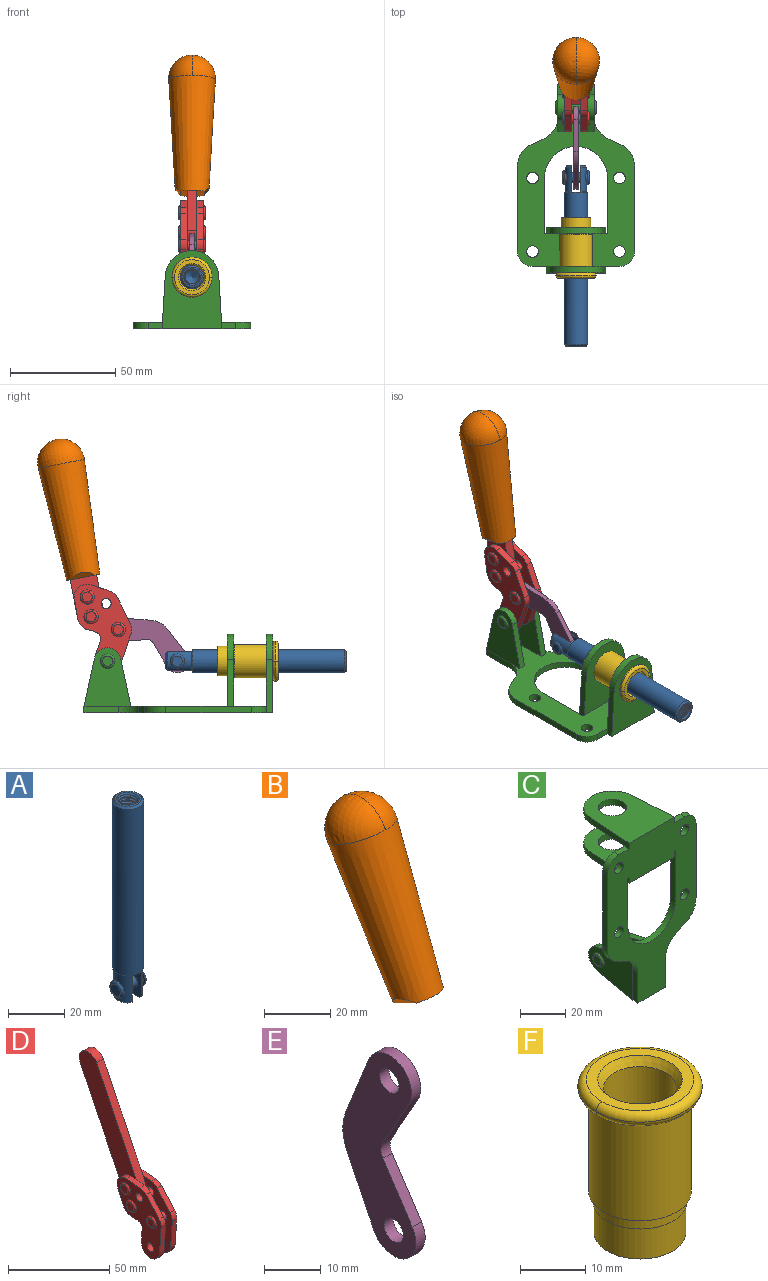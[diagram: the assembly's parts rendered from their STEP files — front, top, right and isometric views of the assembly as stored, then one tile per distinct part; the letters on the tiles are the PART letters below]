
ASSEMBLY  parts=6 mates=6
PART A: 48 faces, bbox 12.6x11.1x86.1 mm
  f0: torus R=2.41mm, axis (-1,0,0), area 15mm2, adj f30,f32,f34
  f1: torus R=2.41mm, axis (-1,0,0), area 15mm2, adj f29,f31,f33
  f2: cylinder r=5.54mm len=72.39mm, axis (0,0,1), area 2518.5mm2, adj f3,f4,f42,f43
  f3: cone r=5.54mm half-angle=45deg, axis (0,0,1), area 7.6mm2, adj f2,f5,f41
  f4: cone r=5.54mm half-angle=45deg, axis (0,0,-1), area 34.9mm2, adj f2,f39
  f5: cylinder r=5.08mm len=11.48mm, axis (0,0,1), area 108.3mm2, adj f3,f7,f8,f41
  f6: cylinder r=2.41mm len=4.83mm, axis (-1,0,0), area 71.2mm2, adj f40,f41
  f7: cylinder r=2.41mm len=4.83mm, axis (-1,0,0), area 7.6mm2, adj f5,f34
  f8: cone r=5.08mm half-angle=45deg, axis (0,0,1), area 10.6mm2, adj f5,f37,f41
  f9: cone r=3.98mm half-angle=45deg, axis (0,0,1), area 17.6mm2, adj f27,f39,f45,f46,f47
  f10: cylinder r=2.41mm len=4.83mm, axis (-1,0,0), area 7.6mm2, adj f33,f38
  f11: cylinder r=3.2mm len=6.4mm, axis (0,0,1), area 78.4mm2, adj f12,f28,f44,f45,f47
  f12: cylinder r=3.2mm len=6.4mm, axis (0,0,1), area 10.5mm2, adj f11,f13,f45,f47
  f13: cylinder r=3.2mm len=6.4mm, axis (0,0,1), area 10.5mm2, adj f12,f14,f45,f47
  f14: cylinder r=3.2mm len=6.4mm, axis (0,0,1), area 10.5mm2, adj f13,f15,f45,f47
  f15: cylinder r=3.2mm len=6.4mm, axis (0,0,1), area 10.5mm2, adj f14,f16,f45,f47
  f16: cylinder r=3.2mm len=6.4mm, axis (0,0,1), area 10.5mm2, adj f15,f17,f45,f47
  f17: cylinder r=3.2mm len=6.4mm, axis (0,0,1), area 10.5mm2, adj f16,f18,f45,f47
  f18: cylinder r=3.2mm len=6.4mm, axis (0,0,1), area 10.5mm2, adj f17,f19,f45,f47
  f19: cylinder r=3.2mm len=6.4mm, axis (0,0,1), area 10.5mm2, adj f18,f20,f45,f47
  f20: cylinder r=3.2mm len=6.4mm, axis (0,0,1), area 10.5mm2, adj f19,f21,f45,f47
  f21: cylinder r=3.2mm len=6.4mm, axis (0,0,1), area 10.5mm2, adj f20,f22,f45,f47
  f22: cylinder r=3.2mm len=6.4mm, axis (0,0,1), area 10.5mm2, adj f21,f23,f45,f47
  f23: cylinder r=3.2mm len=6.4mm, axis (0,0,1), area 10.5mm2, adj f22,f24,f45,f47
  f24: cylinder r=3.2mm len=6.4mm, axis (0,0,1), area 10.5mm2, adj f23,f25,f45,f47
  f25: cylinder r=3.2mm len=6.4mm, axis (0,0,1), area 10.5mm2, adj f24,f26,f45,f47
  f26: cylinder r=3.2mm len=6.4mm, axis (0,0,1), area 10.5mm2, adj f25,f27,f45,f47
  f27: cylinder r=3.2mm len=6.4mm, axis (0,0,1), area 7.4mm2, adj f9,f26,f45,f47
  f28: cone r=3.2mm half-angle=60deg, axis (0,0,1), area 37.2mm2, adj f11
  f29: plane 4.83x4.83mm, normal (-1,0,0), area 18.3mm2, adj f1,f31
  f30: plane 4.83x4.83mm, normal (1,0,0), area 18.3mm2, adj f0,f32
  f31: torus R=2.41mm, axis (-1,0,0), area 15mm2, adj f1,f29,f33
  f32: torus R=2.41mm, axis (-1,0,0), area 15mm2, adj f0,f30,f34
  f33: plane 6.83x6.83mm, normal (1,0,0), area 18.3mm2, adj f1,f10,f31
  f34: plane 6.83x6.83mm, normal (-1,0,0), area 18.3mm2, adj f0,f7,f32
  f35: cone r=5.08mm half-angle=45deg, axis (0,0,1), area 10.6mm2, adj f36,f38,f40
  f36: plane 7.25x1.97mm, normal (0,0,-1), area 10mm2, adj f35,f40
  f37: plane 7.25x1.97mm, normal (0,0,-1), area 10mm2, adj f8,f41
  f38: cylinder r=5.08mm len=11.48mm, axis (0,0,1), area 108.3mm2, adj f10,f35,f40,f42
  f39: plane 9.55x9.55mm, normal (0,0,1), area 22mm2, adj f4,f9
  f40: plane 12.76x10.09mm, normal (1,0,0), area 95.7mm2, adj f6,f35,f36,f38,f42,f43
  f41: plane 12.76x10.09mm, normal (-1,0,0), area 95.7mm2, adj f3,f5,f6,f8,f37,f43
  f42: cone r=5.54mm half-angle=45deg, axis (0,0,1), area 7.6mm2, adj f2,f38,f40
  f43: plane 11.07x4.7mm, normal (0,0,-1), area 50.4mm2, adj f2,f40,f41
  f44: plane 0.89x0.62mm, normal (-1,0,0), area 0.3mm2, adj f11,f45,f46,f47
  f45: bspline ~24.8x7.63mm, area 266.6mm2, adj f9,f11,f12,f13,f14,f15,f16,f17
  f46: bspline ~24.87x7.63mm, area 73.6mm2, adj f9,f44,f45,f47
  f47: bspline ~24.98x7.63mm, area 272.5mm2, adj f9,f11,f12,f13,f14,f15,f16,f17
PART B: 11 faces, bbox 22.3x42.6x64.5 mm
  f0: sphere r=11.13mm, area 411.4mm2, adj f1,f8
  f1: cone r=11.11mm half-angle=3.3deg, axis (0,0.44,0.9), area 3251.8mm2, adj f0,f7,f8,f9,f10
  f2: cylinder r=6.16mm len=11.7mm, axis (1,0,0), area 89.5mm2, adj f3,f4,f5,f6
  f3: plane 60.23x36.75mm, normal (-1,0,0), area 763.6mm2, adj f2,f4,f6,f10
  f4: plane 51.37x25.05mm, normal (0,0.9,-0.44), area 264.2mm2, adj f2,f3,f5,f10
  f5: plane 60.23x36.75mm, normal (1,0,0), area 763.6mm2, adj f2,f4,f6,f10
  f6: plane 51.37x25.05mm, normal (0,-0.9,0.44), area 264.2mm2, adj f2,f3,f5,f10
  f7: plane 9.95x5.95mm, normal (0.71,-0.31,-0.64), area 25.8mm2, adj f1,f10
  f8: sphere r=11.13mm, area 411.4mm2, adj f0,f1
  f9: plane 9.95x5.95mm, normal (-0.71,-0.31,-0.64), area 25.8mm2, adj f1,f10
  f10: plane 14.27x11.38mm, normal (0,-0.44,-0.9), area 106.7mm2, adj f1,f3,f4,f5,f6,f7,f9
PART C: 55 faces, bbox 55.7x37.4x89.8 mm
  f0: torus R=2.41mm, axis (-1,0,0), area 15mm2, adj f11,f15,f25
  f1: torus R=2.41mm, axis (-1,0,0), area 15mm2, adj f10,f12,f22
  f2: cylinder r=2.78mm len=5.56mm, axis (0,-1,0), area 54.2mm2, adj f30,f54
  f3: cylinder r=14.99mm len=29.97mm, axis (0,-1,0), area 145.9mm2, adj f30,f49,f53,f54
  f4: cylinder r=2.78mm len=5.56mm, axis (0,-1,0), area 54.2mm2, adj f30,f54
  f5: cylinder r=2.78mm len=5.56mm, axis (0,-1,0), area 54.2mm2, adj f30,f54
  f6: cylinder r=2.78mm len=5.56mm, axis (0,-1,0), area 54.2mm2, adj f30,f54
  f7: cylinder r=6.35mm len=12.7mm, axis (0,0,1), area 123.6mm2, adj f27,f51
  f8: cylinder r=6.35mm len=12.7mm, axis (0,0,-1), area 124.7mm2, adj f21,f35
  f9: cylinder r=2.41mm len=11.18mm, axis (-1,0,0), area 169.4mm2, adj f16,f19
  f10: plane 4.83x4.83mm, normal (1,0,0), area 18.3mm2, adj f1,f12
  f11: plane 4.83x4.83mm, normal (-1,0,0), area 18.3mm2, adj f0,f15
  f12: torus R=2.41mm, axis (-1,0,0), area 15mm2, adj f1,f10,f22
  f13: cylinder r=6.35mm len=12.41mm, axis (1,0,0), area 53.4mm2, adj f18,f19,f22,f23
  f14: cylinder r=6.35mm len=12.41mm, axis (-1,0,0), area 53.4mm2, adj f16,f17,f24,f25
  f15: torus R=2.41mm, axis (-1,0,0), area 15mm2, adj f0,f11,f25
  f16: plane 27.86x22.35mm, normal (1,0,0), area 425.4mm2, adj f9,f14,f17,f24,f30
  f17: plane 22.86x4.97mm, normal (0,0.21,0.98), area 72.5mm2, adj f14,f16,f25,f30
  f18: plane 22.86x4.97mm, normal (0,0.21,0.98), area 72.5mm2, adj f13,f19,f22,f30
  f19: plane 27.86x22.35mm, normal (-1,0,0), area 425.4mm2, adj f9,f13,f18,f23,f30
  f20: cylinder r=12.7mm len=25.35mm, axis (0,0,-1), area 119.8mm2, adj f21,f34,f35,f36
  f21: plane 34.21x28.07mm, normal (0,0,-1), area 702.4mm2, adj f8,f20,f30,f34,f36
  f22: plane 27.96x22.45mm, normal (1,0,0), area 407.2mm2, adj f1,f12,f13,f18,f23,f30,f42,f43
  f23: plane 22.86x4.97mm, normal (0,0.21,-0.98), area 72.5mm2, adj f13,f19,f22,f44
  f24: plane 22.86x4.97mm, normal (0,0.21,-0.98), area 72.5mm2, adj f14,f16,f25,f44
  f25: plane 27.86x22.35mm, normal (-1,0,0), area 407.1mm2, adj f0,f14,f15,f17,f24,f30,f45,f46
  f26: plane 3.1x0.95mm, normal (0,0,-1), area 2.7mm2, adj f30,f49,f50,f54
  f27: plane 34.21x28.07mm, normal (0,0,1), area 702.4mm2, adj f7,f28,f30,f50,f52
  f28: cylinder r=12.7mm len=25.35mm, axis (0,0,1), area 118.8mm2, adj f27,f50,f51,f52
  f29: plane 3.1x0.95mm, normal (0,0,-1), area 2.7mm2, adj f30,f52,f53,f54
  f30: plane 86.54x55.63mm, normal (0,1,0), area 2362.9mm2, adj f2,f3,f4,f5,f6,f16,f17,f18
  f31: plane 40.56x3.1mm, normal (-1,0,0), area 125.7mm2, adj f30,f32,f48,f54
  f32: cylinder r=7.11mm len=7.11mm, axis (0,-1,0), area 34.6mm2, adj f30,f31,f33,f54
  f33: plane 6.67x3.1mm, normal (0,0,1), area 20.4mm2, adj f30,f32,f34,f54
  f34: plane 25.39x3.13mm, normal (-1,0.06,0), area 79.5mm2, adj f20,f21,f33,f35,f54
  f35: plane 37.31x28.45mm, normal (0,0,1), area 789.9mm2, adj f8,f20,f34,f36,f54
  f36: plane 25.39x3.13mm, normal (1,0.06,0), area 79.5mm2, adj f20,f21,f35,f37,f54
  f37: plane 6.67x3.1mm, normal (0,0,1), area 20.4mm2, adj f30,f36,f38,f54
  f38: cylinder r=7.11mm len=7.11mm, axis (0,-1,0), area 34.6mm2, adj f30,f37,f39,f54
  f39: plane 40.56x3.1mm, normal (1,0,0), area 125.7mm2, adj f30,f38,f40,f54
  f40: cylinder r=11.18mm len=10.16mm, axis (0,-1,0), area 39.5mm2, adj f30,f39,f41,f54
  f41: plane 6.09x3.1mm, normal (0.42,0,-0.91), area 20.8mm2, adj f30,f40,f42,f54
  f42: cylinder r=11.18mm len=9.41mm, axis (0,-1,0), area 37.2mm2, adj f22,f30,f41,f43,f54
  f43: plane 16.5x3.1mm, normal (1,0,0), area 51.1mm2, adj f22,f42,f44,f54
  f44: plane 17.37x3.1mm, normal (0,0,-1), area 53.8mm2, adj f23,f24,f30,f43,f45,f54
  f45: plane 16.5x3.1mm, normal (-1,0,0), area 51.1mm2, adj f25,f44,f46,f54
  f46: cylinder r=11.18mm len=9.41mm, axis (0,-1,0), area 37.2mm2, adj f25,f30,f45,f47,f54
  f47: plane 6.09x3.1mm, normal (-0.42,0,-0.91), area 20.8mm2, adj f30,f46,f48,f54
  f48: cylinder r=11.18mm len=10.16mm, axis (0,-1,0), area 39.5mm2, adj f30,f31,f47,f54
  f49: plane 26.54x3.1mm, normal (-1,0,0), area 82.3mm2, adj f3,f26,f30,f54
  f50: plane 25.39x3.1mm, normal (1,0.06,0), area 78.8mm2, adj f26,f27,f28,f51,f54
  f51: plane 37.31x28.45mm, normal (0,0,-1), area 789.9mm2, adj f7,f28,f50,f52,f54
  f52: plane 25.39x3.1mm, normal (-1,0.06,0), area 78.8mm2, adj f27,f28,f29,f51,f54
  f53: plane 26.54x3.1mm, normal (1,0,0), area 82.3mm2, adj f3,f29,f30,f54
  f54: plane 89.66x55.63mm, normal (0,-1,0), area 2678.5mm2, adj f2,f3,f4,f5,f6,f26,f29,f31
PART D: 59 faces, bbox 12.9x60.2x99.6 mm
  f0: torus R=2.39mm, axis (-1,0,0), area 14.9mm2, adj f20,f43,f51
  f1: torus R=2.39mm, axis (-1,0,0), area 14.9mm2, adj f19,f42,f51
  f2: torus R=2.39mm, axis (-1,0,0), area 14.9mm2, adj f18,f35,f51
  f3: torus R=2.39mm, axis (-1,0,0), area 14.9mm2, adj f14,f17,f23
  f4: torus R=2.39mm, axis (-1,0,0), area 14.9mm2, adj f13,f16,f23
  f5: torus R=2.39mm, axis (-1,0,0), area 14.9mm2, adj f12,f15,f23
  f6: cylinder r=2.39mm len=4.78mm, axis (1,0,0), area 46.5mm2, adj f48,f50,f51
  f7: cylinder r=2.39mm len=4.78mm, axis (1,0,0), area 46.5mm2, adj f50,f51
  f8: cylinder r=6.35mm len=12.68mm, axis (1,0,0), area 61.8mm2, adj f38,f39,f50,f51
  f9: cylinder r=2.39mm len=4.78mm, axis (-1,0,0), area 70.5mm2, adj f46,f50
  f10: cylinder r=2.39mm len=4.78mm, axis (-1,0,0), area 46.5mm2, adj f23,f45,f46
  f11: cylinder r=2.39mm len=4.78mm, axis (-1,0,0), area 46.5mm2, adj f23,f46
  f12: plane 4.78x4.78mm, normal (1,0,0), area 17.9mm2, adj f5,f15
  f13: plane 4.78x4.78mm, normal (1,0,0), area 17.9mm2, adj f4,f16
  f14: plane 4.78x4.78mm, normal (1,0,0), area 17.9mm2, adj f3,f17
  f15: torus R=2.39mm, axis (-1,0,0), area 14.9mm2, adj f5,f12,f23
  f16: torus R=2.39mm, axis (-1,0,0), area 14.9mm2, adj f4,f13,f23
  f17: torus R=2.39mm, axis (-1,0,0), area 14.9mm2, adj f3,f14,f23
  f18: plane 4.78x4.78mm, normal (-1,0,0), area 17.9mm2, adj f2,f35
  f19: plane 4.78x4.78mm, normal (-1,0,0), area 17.9mm2, adj f1,f42
  f20: plane 4.78x4.78mm, normal (-1,0,0), area 17.9mm2, adj f0,f43
  f21: plane 2.26x0.2mm, normal (1,0,0), area 0.2mm2, adj f31,f44
  f22: plane 2.26x0.2mm, normal (-1,0,0), area 0.2mm2, adj f41,f44
  f23: plane 39.37x30.77mm, normal (1,0,0), area 565.5mm2, adj f3,f4,f5,f10,f11,f15,f16,f17
  f24: cylinder r=6.1mm len=4.15mm, axis (-1,0,0), area 14.7mm2, adj f23,f25,f32,f46
  f25: plane 10.25x9.01mm, normal (0,-0.75,0.66), area 42.3mm2, adj f23,f24,f26,f46
  f26: cylinder r=6.35mm len=4.64mm, axis (-1,0,0), area 15.6mm2, adj f23,f25,f27,f46
  f27: plane 15.84x3.1mm, normal (0,-1,-0.07), area 49.2mm2, adj f23,f26,f28,f46
  f28: cylinder r=6.35mm len=12.68mm, axis (-1,0,0), area 61.8mm2, adj f23,f27,f29,f46
  f29: plane 8.11x3.1mm, normal (0,1,0.07), area 25.2mm2, adj f23,f28,f30,f46
  f30: cylinder r=3.05mm len=3.25mm, axis (-1,0,0), area 14.8mm2, adj f23,f29,f31,f46
  f31: plane 5.99x3.1mm, normal (0,0.07,-1), area 18.6mm2, adj f21,f23,f30,f44,f46
  f32: plane 9.5x3.1mm, normal (0,-0.07,1), area 29.5mm2, adj f23,f24,f33,f46,f47
  f33: cylinder r=6.1mm len=8.63mm, axis (-1,0,0), area 39.1mm2, adj f23,f32,f34,f47
  f34: plane 8.65x3.96mm, normal (0,0.91,-0.42), area 29.5mm2, adj f23,f33,f44,f47
  f35: torus R=2.39mm, axis (-1,0,0), area 14.9mm2, adj f2,f18,f51
  f36: plane 10.25x9.01mm, normal (0,-0.75,0.66), area 42.3mm2, adj f37,f49,f50,f51
  f37: cylinder r=6.35mm len=4.64mm, axis (1,0,0), area 15.6mm2, adj f36,f38,f50,f51
  f38: plane 15.84x3.1mm, normal (0,-1,-0.07), area 49.2mm2, adj f8,f37,f50,f51
  f39: plane 8.11x3.1mm, normal (0,1,0.07), area 25.2mm2, adj f8,f40,f50,f51
  f40: cylinder r=3.05mm len=3.25mm, axis (1,0,0), area 14.8mm2, adj f39,f41,f50,f51
  f41: plane 5.99x3.1mm, normal (0,0.07,-1), area 18.6mm2, adj f22,f40,f44,f50,f51
  f42: torus R=2.39mm, axis (-1,0,0), area 14.9mm2, adj f1,f19,f51
  f43: torus R=2.39mm, axis (-1,0,0), area 14.9mm2, adj f0,f20,f51
  f44: cylinder r=6.35mm len=12.12mm, axis (-1,0,0), area 128.9mm2, adj f21,f22,f23,f31,f34,f41,f46,f47
  f45: plane 2.65x1.35mm, normal (1,0,0), area 1mm2, adj f10,f55
  f46: plane 39.08x20.42mm, normal (-1,0,0), area 412.5mm2, adj f9,f10,f11,f24,f25,f26,f27,f28
  f47: plane 77.62x39.82mm, normal (1,0,0), area 850mm2, adj f32,f33,f34,f44,f53,f54,f55
  f48: plane 2.65x1.35mm, normal (-1,0,0), area 1mm2, adj f6,f55
  f49: cylinder r=6.1mm len=4.15mm, axis (1,0,0), area 14.7mm2, adj f36,f50,f51,f56
  f50: plane 39.08x20.42mm, normal (1,0,0), area 412.5mm2, adj f6,f7,f8,f9,f36,f37,f38,f39
  f51: plane 39.37x30.77mm, normal (-1,0,0), area 565.5mm2, adj f0,f1,f2,f6,f7,f8,f35,f36
  f52: plane 8.65x3.96mm, normal (0,0.91,-0.42), area 29.5mm2, adj f44,f51,f57,f58
  f53: plane 68.49x33.4mm, normal (0,0.9,-0.44), area 358.1mm2, adj f44,f47,f54,f58
  f54: cylinder r=6.35mm len=12.06mm, axis (1,0,0), area 93.7mm2, adj f47,f53,f55,f58
  f55: plane 68.49x33.4mm, normal (0,-0.9,0.44), area 358.1mm2, adj f44,f45,f46,f47,f48,f50,f54,f58
  f56: plane 9.5x3.1mm, normal (0,-0.07,1), area 29.5mm2, adj f49,f50,f51,f57,f58
  f57: cylinder r=6.1mm len=8.63mm, axis (1,0,0), area 39.1mm2, adj f51,f52,f56,f58
  f58: plane 77.62x39.82mm, normal (-1,0,0), area 850mm2, adj f44,f52,f53,f54,f55,f56,f57
PART E: 12 faces, bbox 2.3x18.2x42.8 mm
  f0: cylinder r=2.4mm len=4.8mm, axis (1,0,0), area 34.9mm2, adj f4,f11
  f1: cylinder r=10.41mm len=8.47mm, axis (1,0,0), area 20.2mm2, adj f4,f9,f10,f11
  f2: cylinder r=3.05mm len=3.16mm, axis (1,0,0), area 7.7mm2, adj f4,f6,f7,f11
  f3: cylinder r=2.4mm len=4.8mm, axis (1,0,0), area 34.9mm2, adj f4,f11
  f4: plane 42.81x18.23mm, normal (-1,0,0), area 414.1mm2, adj f0,f1,f2,f3,f5,f6,f7,f8
  f5: cylinder r=5.54mm len=10.67mm, axis (1,0,0), area 41.8mm2, adj f4,f6,f10,f11
  f6: plane 11.66x6.53mm, normal (0,-0.87,-0.49), area 30.9mm2, adj f2,f4,f5,f11
  f7: plane 11.17x7.33mm, normal (0,-0.84,0.55), area 30.9mm2, adj f2,f4,f8,f11
  f8: cylinder r=5.54mm len=10.51mm, axis (1,0,0), area 41.8mm2, adj f4,f7,f9,f11
  f9: plane 13.67x6.67mm, normal (0,0.9,-0.44), area 35.1mm2, adj f1,f4,f8,f11
  f10: plane 14.1x5.7mm, normal (0,0.93,0.37), area 35.1mm2, adj f1,f4,f5,f11
  f11: plane 42.81x18.23mm, normal (1,0,0), area 414.1mm2, adj f0,f1,f2,f3,f5,f6,f7,f8
PART F: 15 faces, bbox 20.6x20.6x28.7 mm
  f0: torus R=8.26mm, axis (0,0,1), area 56.8mm2, adj f1,f10,f12
  f1: torus R=8.26mm, axis (0,0,1), area 56.8mm2, adj f0,f6,f13
  f2: cylinder r=5.59mm len=25.91mm, axis (0,0,1), area 909.6mm2, adj f3,f4
  f3: cone r=6.86mm half-angle=45deg, axis (0,0,-1), area 70.2mm2, adj f2,f14
  f4: cone r=6.47mm half-angle=30deg, axis (0,0,1), area 66.7mm2, adj f2,f13
  f5: cylinder r=7.04mm len=14.07mm, axis (0,0,1), area 252.6mm2, adj f11,f14
  f6: torus R=8.26mm, axis (0,0,1), area 56.8mm2, adj f1,f12,f13
  f7: cylinder r=7.16mm len=14.33mm, axis (0,0,1), area 91.5mm2, adj f9,f11
  f8: cylinder r=7.86mm len=18.42mm, axis (0,0,1), area 909.6mm2, adj f9,f10
  f9: plane 15.72x15.72mm, normal (0,0,-1), area 33mm2, adj f7,f8
  f10: plane 16.51x16.51mm, normal (0,0,-1), area 19.9mm2, adj f0,f8,f12
  f11: plane 14.33x14.33mm, normal (0,0,-1), area 5.7mm2, adj f5,f7
  f12: torus R=8.26mm, axis (0,0,1), area 56.8mm2, adj f0,f6,f10
  f13: plane 16.51x16.51mm, normal (0,0,1), area 82.7mm2, adj f1,f4,f6
  f14: plane 14.07x14.07mm, normal (0,0,-1), area 7.8mm2, adj f3,f5
PLACE A rot(axis=(1,0,0),90deg) t=(0,15.65,-3.1)mm
PLACE B rot(axis=(1,0,0),15deg) t=(0.04,1.24,46.14)mm
PLACE C rot(axis=(1,0,0),90deg) t=(0,1.23,-3.1)mm fixed
PLACE D rot(axis=(1,0,0),15deg) t=(0,1.24,46.14)mm
PLACE E rot(axis=(1,0,0),120.2deg) t=(0,25.94,8.03)mm
PLACE F rot(axis=(1,0,0),90deg) t=(0,1.23,-3.1)mm
MATE revolute E.f5 <-> A.f6  axis (1,0,0) through (0,0.18,21.51)mm
MATE revolute E.f3 <-> D.f4  axis (1,0,0) through (0,28.16,36.52)mm
MATE fastened B.f2 <-> D.f54  axis (-1,0,0) through (2.35,55.69,117.44)mm
MATE revolute D.f7 <-> C.f0  axis (1,0,0) through (0,33.32,21.51)mm
MATE slider A.f2 <-> F.f2  axis (0,-1,0) through (0,-43.13,21.51)mm
MATE fastened C.f7 <-> F.f0  axis (0,-1,0) through (0,-45.16,21.51)mm
